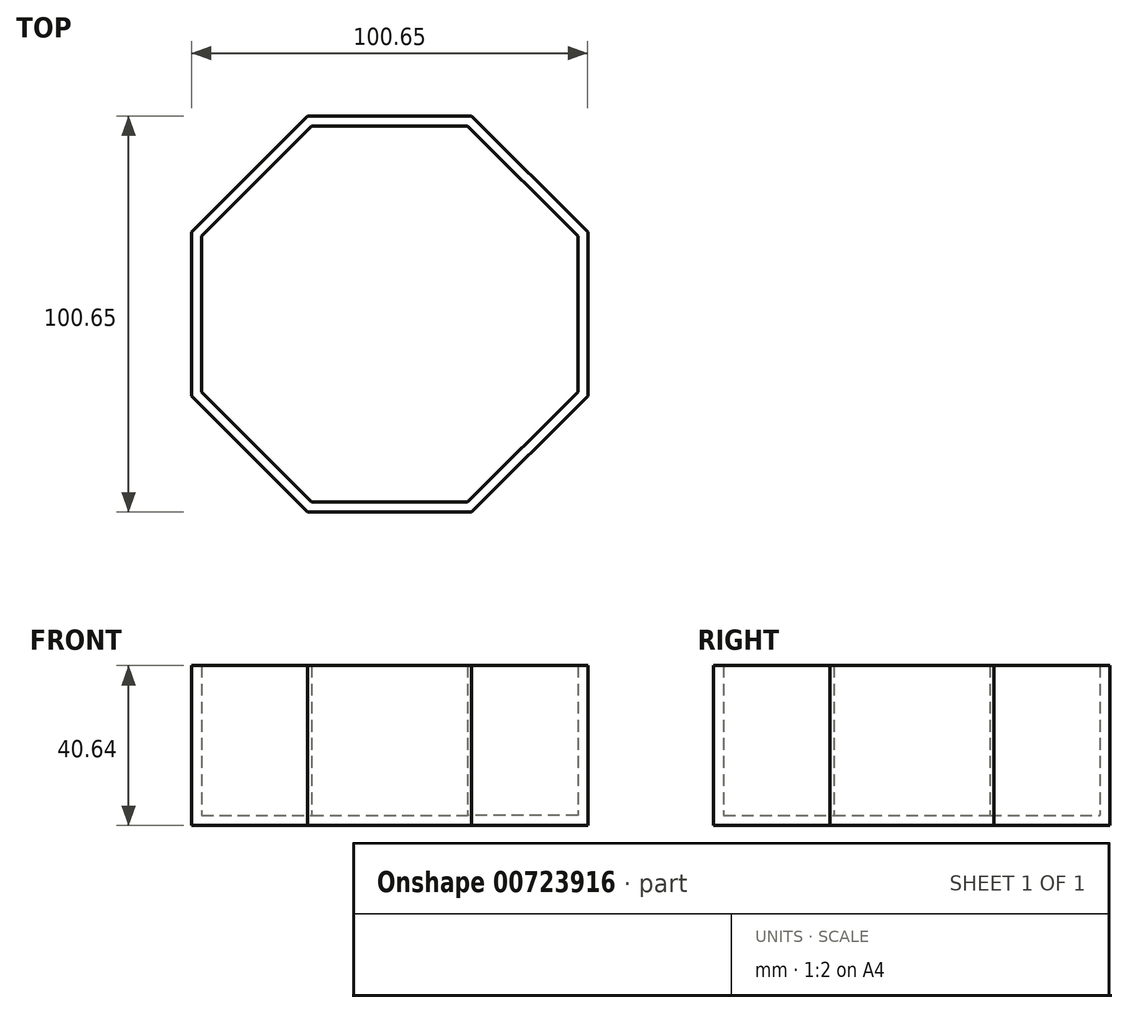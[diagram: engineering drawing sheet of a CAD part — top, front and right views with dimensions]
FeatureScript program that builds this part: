
annotation { "Feature Type Name" : "Feature", "Feature Type Description" : "" }
export const myFeature = defineFeature(function(context is Context, id is Id, definition is map)
    precondition{}
    {
        {
            var Q0;
            Q0=qCreatedBy(makeId("Top.planeOp"),FACE);
            var sketch = newSketch(context, id + "F0", { "sketchPlane" : qUnion([Q0])});
            skCircle(sketch, "E0.cCircle", {"center": v(-9.98, -13.13) * mm, "radius": 50.32 * mm, "construction": true});
            skLineSegment(sketch, "E0.0", {"start": v(-30.83, 37.19) * mm, "end": v(10.86, 37.19) * mm});
            skLineSegment(sketch, "E0.1", {"start": v(10.86, 37.19) * mm, "end": v(40.34, 7.71) * mm});
            skLineSegment(sketch, "E0.2", {"start": v(40.34, 7.71) * mm, "end": v(40.34, -33.98) * mm});
            skLineSegment(sketch, "E0.3", {"start": v(40.34, -33.98) * mm, "end": v(10.86, -63.46) * mm});
            skLineSegment(sketch, "E0.4", {"start": v(10.86, -63.46) * mm, "end": v(-30.83, -63.46) * mm});
            skLineSegment(sketch, "E0.5", {"start": v(-30.83, -63.46) * mm, "end": v(-60.3, -33.98) * mm});
            skLineSegment(sketch, "E0.6", {"start": v(-60.3, -33.98) * mm, "end": v(-60.3, 7.71) * mm});
            skLineSegment(sketch, "E0.7", {"start": v(-60.3, 7.71) * mm, "end": v(-30.83, 37.19) * mm});
            skPoint(sketch, "E0.0.midPoint", {"position": v(-9.98, 37.19) * mm});
            skSolve(sketch);
        }
        {
            var Q0;
            Q0 = qSketchRegion(id + "F0", true);
            extrude(context, id + "F1", {"entities" : qUnion([Q0]), "depth" : 40.64 * mm, "offsetDistance" : 25.4 * mm});
        }
        {
            var Q0;
            Q0=makeQuery(id+"F1.opExtrude","CAP_FACE",FACE,{"disambiguationData":[OSD([sQuery(id+"F0.wireOp",EDGE,"E0.0"),sQuery(id+"F0.wireOp",EDGE,"E0.1"),sQuery(id+"F0.wireOp",EDGE,"E0.2"),sQuery(id+"F0.wireOp",EDGE,"E0.3"),sQuery(id+"F0.wireOp",EDGE,"E0.4"),sQuery(id+"F0.wireOp",EDGE,"E0.5"),sQuery(id+"F0.wireOp",EDGE,"E0.6"),sQuery(id+"F0.wireOp",EDGE,"E0.7")])],"isStart":false});
            shell(context, id + "F2", {"entities" : qUnion([Q0]), "thickness" : 2.54 * mm});
        }
    });
